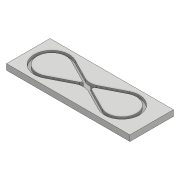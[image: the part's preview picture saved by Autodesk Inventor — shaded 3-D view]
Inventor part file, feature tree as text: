
AUTODESK INVENTOR PART (.ipt)
format: ipt  version: 2017 (Build 210142000, 142)  size: 183,808 bytes
history: native  units: mm
features: extrude x6, sketch x2, boolean_combine x2, fillet x1
ambient origin geometry x8: Origin, YZ Plane, XZ Plane, XY Plane, X Axis, Y Axis, Z Axis, Center Point
bodies: Solid1 (feature_tree), Solid2 (feature_tree), Solid3 (feature_tree), Solid4 (feature_tree), Solid5 (feature_tree)
feature tree (11):
  sketch  "Sketch1"  dims[d3=10.0mm d4=425.0mm]
  extrude  "Extrusion1"  Depth=425.0mm
  extrude  "Extrusion2"  Depth=50.0mm
  extrude  "Extrusion3"  Depth=6.0mm
  extrude  "Extrusion4"  Depth=9.0mm
  fillet  "Fillet1"  Radius=10.0mm
  extrude  "Extrusion5"  Depth=10.0mm TaperAngle=0.0deg
  extrude  "Extrusion6"  Depth=10.0mm TaperAngle=0.0deg
  boolean_combine  "Combine1"
  boolean_combine  "Combine2"
  sketch  "Sketch2"  dims[d5=150.0mm d6=50.0mm d7=6.0mm d8=4.0mm d9=10.0mm d10=0.0mm d11=10.0mm d12=0.0mm d13=10.0mm d14=0.0mm d15=10.0mm d16=0.0mm d17=6.25mm d18=9.0mm d19=0.0mm d20=9.0mm d21=0.0mm]
